annotation { "Feature Type Name" : "Feature", "Feature Type Description" : "" }
export const myFeature = defineFeature(function(context is Context, id is Id, definition is map)
    precondition{}
    {
        {
            var Q0;
            Q0=qCreatedBy(makeId("Top.planeOp"),FACE);
            var sketch = newSketch(context, id + "F0", { "sketchPlane" : qUnion([Q0])});
            skText(sketch, "E0", { "text": "JESSICA ALGER\n57468 BLACKHAWK DR\nGOSHEN, IN 46528\n574-214-2102", "fontName": "NotoSans-Bold.ttf"});
            const initialGuessF0  = {"E0": [-0.01902, 0, 1, 0, 0.00476]};
            skSetInitialGuess(sketch, initialGuessF0);
            skSolve(sketch);
        }
        {
            var Q0;
            Q0=qCreatedBy(makeId("Top.planeOp"),FACE);
            var sketch = newSketch(context, id + "F1", { "sketchPlane" : qUnion([Q0])});
            skLineSegment(sketch, "E1.bottom", {"start": v(-22.2, 7.94) * mm, "end": v(58.45, 7.94) * mm});
            skLineSegment(sketch, "E1.top", {"start": v(-22.2, -30.16) * mm, "end": v(58.45, -30.16) * mm});
            skLineSegment(sketch, "E1.left", {"start": v(-22.2, 7.94) * mm, "end": v(-22.2, -30.16) * mm});
            skLineSegment(sketch, "E1.right", {"start": v(58.45, 7.94) * mm, "end": v(58.45, -30.16) * mm});
            skSolve(sketch);
        }
        {
            var Q0;
            Q0 = qSketchRegion(id + "F1", true);
            extrude(context, id + "F2", {"entities" : qUnion([Q0]), "depth" : 3.17 * mm, "offsetDistance" : 25.4 * mm});
        }
        {
            var Q0;
            Q0 = qSketchRegion(id + "F0", true);
            var Q1;
            Q1=makeQuery(id+"F2.opExtrude","CAP_FACE",FACE,{"disambiguationData":[OSD([sQuery(id+"F1.wireOp",EDGE,"E1.bottom"),sQuery(id+"F1.wireOp",EDGE,"E1.top"),sQuery(id+"F1.wireOp",EDGE,"E1.left"),sQuery(id+"F1.wireOp",EDGE,"E1.right")])],"isStart":false});
            extrude(context, id + "F3", {"entities" : qUnion([Q0]), "operationType" : NewBodyOperationType.REMOVE, "depth" : 25.4 * mm, "endBoundEntityFace" : qUnion([Q1]), "hasOffset" : true, "offsetDistance" : 1.59 * mm});
        }
        {
            var Q0;
            Q0 = qSketchRegion(id + "F0", true);
            extrude(context, id + "F4", {"entities" : qUnion([Q0]), "operationType" : NewBodyOperationType.ADD, "depth" : 1.59 * mm, "offsetDistance" : 25.4 * mm});
        }
        {
            var Q0;
            Q0=makeQuery(id+"F2.opExtrude","SWEPT_EDGE",EDGE,{"disambiguationData":[OSD([sQuery(id+"F1.wireOp",EDGE,"E1.top"),sQuery(id+"F1.wireOp",EDGE,"E1.right")])]});
            var Q1;
            Q1=makeQuery(id+"F2.opExtrude","SWEPT_EDGE",EDGE,{"disambiguationData":[OSD([sQuery(id+"F1.wireOp",EDGE,"E1.bottom"),sQuery(id+"F1.wireOp",EDGE,"E1.right")])]});
            var Q2;
            Q2=makeQuery(id+"F2.opExtrude","SWEPT_EDGE",EDGE,{"disambiguationData":[OSD([sQuery(id+"F1.wireOp",EDGE,"E1.bottom"),sQuery(id+"F1.wireOp",EDGE,"E1.left")])]});
            var Q3;
            Q3=makeQuery(id+"F2.opExtrude","SWEPT_EDGE",EDGE,{"disambiguationData":[OSD([sQuery(id+"F1.wireOp",EDGE,"E1.top"),sQuery(id+"F1.wireOp",EDGE,"E1.left")])]});
            fillet(context, id + "F5", {"entities" : qUnion([Q0, Q1, Q2, Q3]), "radius" : 5.08 * mm, "tangentPropagation" : true, "allowEdgeOverflow" : false});
        }
        {
            var Q0;
            {var subQ0=sQuery(id+"F1.wireOp",EDGE,"E1.right");var subQ1=sQuery(id+"F1.wireOp",EDGE,"E1.bottom");var subQ2=sQuery(id+"F1.wireOp",EDGE,"E1.top");var subQ3=sQuery(id+"F1.wireOp",EDGE,"E1.left");Q0=makeQuery(id+"F3.boolean.opBoolean","SPLIT",FACE,{"disambiguationData":[TD([makeQuery(id+"F2.opExtrude","SWEPT_FACE",FACE,{"disambiguationData":[OSD([subQ1])]})])],"derivedFrom":makeQuery(id+"F2.opExtrude","CAP_FACE",FACE,{"disambiguationData":[OSD([subQ1,subQ2,subQ3,subQ0])],"isStart":false})});}
            var sketch = newSketch(context, id + "F6", { "sketchPlane" : qUnion([Q0])});
            skCircle(sketch, "E2.1.0.0", {"center": v(52.81, -24.6) * mm, "radius": 1.59 * mm});
            skCircle(sketch, "E3", {"center": v(52.81, -21.43) * mm, "radius": 1.59 * mm});
            skLineSegment(sketch, "E4", {"start": v(52.81, -21.43) * mm, "end": v(52.81, -24.6) * mm});
            skLineSegment(sketch, "E5", {"start": v(51.23, -21.57) * mm, "end": v(51.23, -24.47) * mm});
            skLineSegment(sketch, "E6", {"start": v(54.4, -21.45) * mm, "end": v(54.4, -24.59) * mm});
            skSolve(sketch);
        }
        {
            var Q0;
            Q0 = qSketchRegion(id + "F6", true);
            extrude(context, id + "F7", {"entities" : qUnion([Q0]), "operationType" : NewBodyOperationType.REMOVE, "endBound" : BoundingType.THROUGH_ALL, "oppositeDirection" : true, "depth" : 25.4 * mm, "offsetDistance" : 25.4 * mm});
        }
    });